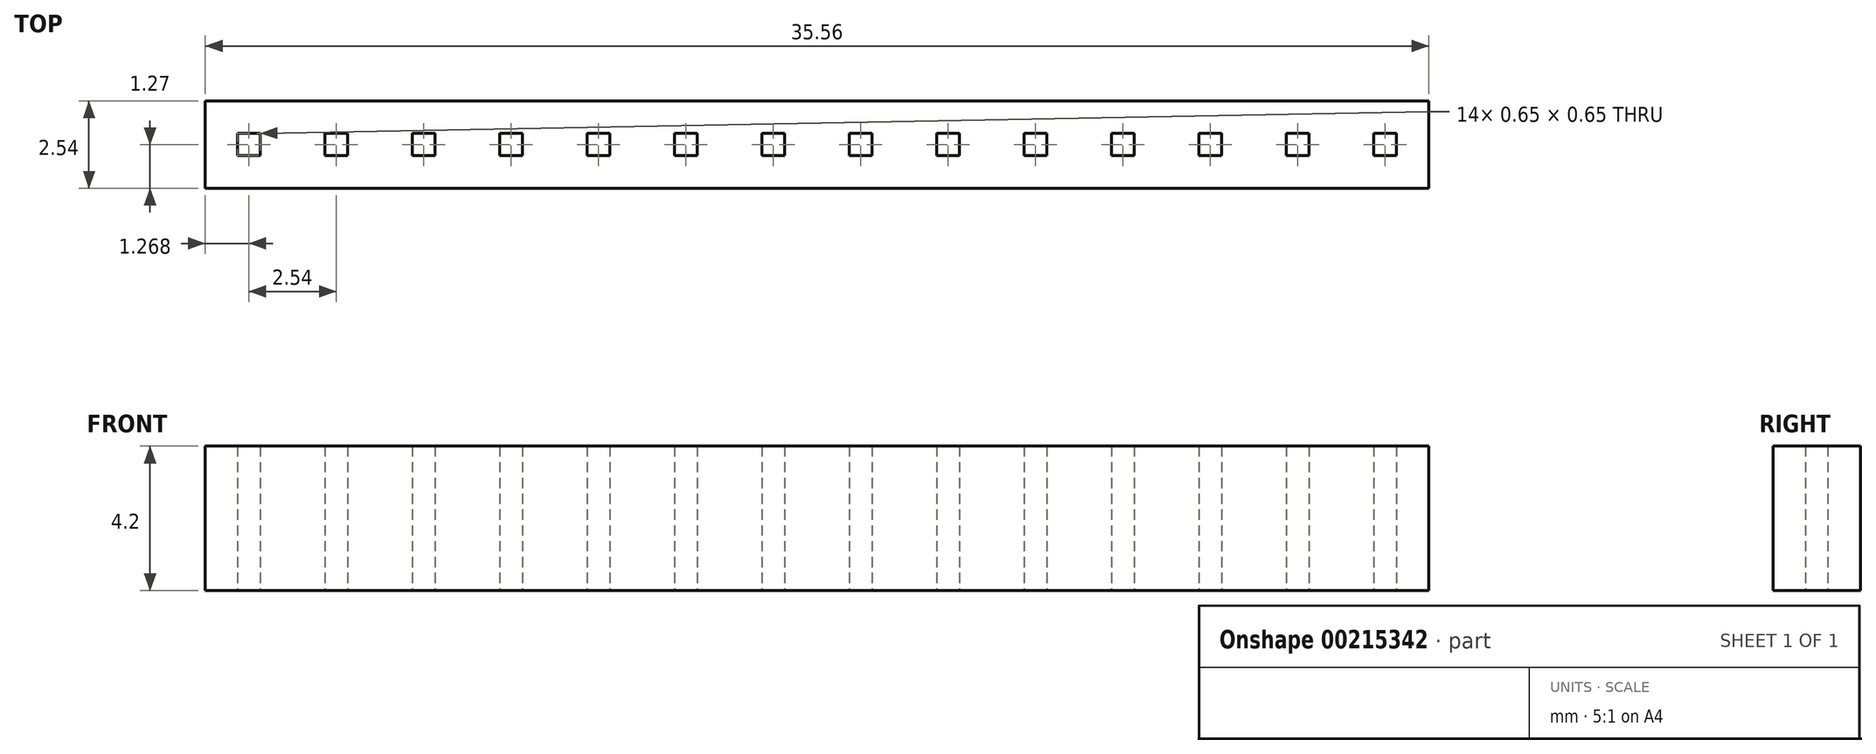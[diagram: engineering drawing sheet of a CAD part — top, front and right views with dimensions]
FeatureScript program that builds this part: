
annotation { "Feature Type Name" : "Feature", "Feature Type Description" : "" }
export const myFeature = defineFeature(function(context is Context, id is Id, definition is map)
    precondition{}
    {
        {
            var Q0;
            Q0=qCreatedBy(makeId("Top.planeOp"),FACE);
            var sketch = newSketch(context, id + "F0", { "sketchPlane" : qUnion([Q0])});
            skLineSegment(sketch, "E0.bottom", {"start": v(-68.73, 0) * mm, "end": v(-71.27, 0) * mm});
            skLineSegment(sketch, "E0.top", {"start": v(-68.73, 2.54) * mm, "end": v(-71.27, 2.54) * mm});
            skLineSegment(sketch, "E0.left", {"start": v(-68.73, 0) * mm, "end": v(-68.73, 2.54) * mm});
            skLineSegment(sketch, "E0.right", {"start": v(-71.27, 0) * mm, "end": v(-71.27, 2.54) * mm});
            skPoint(sketch, "E0.middle", {"position": v(-70, 1.27) * mm});
            skLineSegment(sketch, "E1.left", {"start": v(-68.73, 0.4) * mm, "end": v(-68.73, 1.6) * mm});
            skLineSegment(sketch, "E2.bottom", {"start": v(-70.33, 1.6) * mm, "end": v(-69.68, 1.6) * mm});
            skLineSegment(sketch, "E2.top", {"start": v(-70.33, 0.94) * mm, "end": v(-69.68, 0.94) * mm});
            skLineSegment(sketch, "E2.left", {"start": v(-70.33, 1.6) * mm, "end": v(-70.33, 0.94) * mm});
            skLineSegment(sketch, "E2.right", {"start": v(-69.68, 1.6) * mm, "end": v(-69.68, 0.94) * mm});
            skLineSegment(sketch, "E3.1.0.0", {"start": v(-66.2, 0) * mm, "end": v(-68.73, 0) * mm});
            skLineSegment(sketch, "E3.1.0.1", {"start": v(-66.2, 2.54) * mm, "end": v(-68.73, 2.54) * mm});
            skPoint(sketch, "E3.1.0.2", {"position": v(-67.46, 1.27) * mm});
            skLineSegment(sketch, "E3.1.0.3", {"start": v(-66.2, 0.4) * mm, "end": v(-66.2, 1.6) * mm});
            skPoint(sketch, "E3.1.0.4", {"position": v(-67.46, 1.27) * mm});
            skLineSegment(sketch, "E3.1.0.5", {"start": v(-66.2, 0) * mm, "end": v(-66.2, 2.54) * mm});
            skLineSegment(sketch, "E3.1.0.7", {"start": v(-67.14, 1.6) * mm, "end": v(-67.14, 0.94) * mm});
            skLineSegment(sketch, "E3.1.0.8", {"start": v(-67.79, 1.6) * mm, "end": v(-67.79, 0.94) * mm});
            skLineSegment(sketch, "E3.1.0.9", {"start": v(-67.79, 1.6) * mm, "end": v(-67.14, 1.6) * mm});
            skLineSegment(sketch, "E3.1.0.10", {"start": v(-67.79, 0.94) * mm, "end": v(-67.14, 0.94) * mm});
            skLineSegment(sketch, "E3.2.0.0", {"start": v(-63.65, 0) * mm, "end": v(-66.2, 0) * mm});
            skLineSegment(sketch, "E3.2.0.1", {"start": v(-63.65, 2.54) * mm, "end": v(-66.2, 2.54) * mm});
            skPoint(sketch, "E3.2.0.2", {"position": v(-64.92, 1.27) * mm});
            skLineSegment(sketch, "E3.2.0.3", {"start": v(-63.65, 0.4) * mm, "end": v(-63.65, 1.6) * mm});
            skPoint(sketch, "E3.2.0.4", {"position": v(-64.92, 1.27) * mm});
            skLineSegment(sketch, "E3.2.0.5", {"start": v(-63.65, 0) * mm, "end": v(-63.65, 2.54) * mm});
            skLineSegment(sketch, "E3.2.0.6", {"start": v(-66.2, 0) * mm, "end": v(-66.2, 2.54) * mm});
            skLineSegment(sketch, "E3.2.0.7", {"start": v(-64.6, 1.6) * mm, "end": v(-64.6, 0.94) * mm});
            skLineSegment(sketch, "E3.2.0.8", {"start": v(-65.25, 1.6) * mm, "end": v(-65.25, 0.94) * mm});
            skLineSegment(sketch, "E3.2.0.9", {"start": v(-65.25, 1.6) * mm, "end": v(-64.6, 1.6) * mm});
            skLineSegment(sketch, "E3.2.0.10", {"start": v(-65.25, 0.94) * mm, "end": v(-64.6, 0.94) * mm});
            skLineSegment(sketch, "E3.3.0.0", {"start": v(-61.11, 0) * mm, "end": v(-63.65, 0) * mm});
            skLineSegment(sketch, "E3.3.0.1", {"start": v(-61.11, 2.54) * mm, "end": v(-63.65, 2.54) * mm});
            skPoint(sketch, "E3.3.0.2", {"position": v(-62.38, 1.27) * mm});
            skLineSegment(sketch, "E3.3.0.3", {"start": v(-61.11, 0.4) * mm, "end": v(-61.11, 1.6) * mm});
            skPoint(sketch, "E3.3.0.4", {"position": v(-62.38, 1.27) * mm});
            skLineSegment(sketch, "E3.3.0.5", {"start": v(-61.11, 0) * mm, "end": v(-61.11, 2.54) * mm});
            skLineSegment(sketch, "E3.3.0.6", {"start": v(-63.65, 0) * mm, "end": v(-63.65, 2.54) * mm});
            skLineSegment(sketch, "E3.3.0.7", {"start": v(-62.06, 1.6) * mm, "end": v(-62.06, 0.94) * mm});
            skLineSegment(sketch, "E3.3.0.8", {"start": v(-62.7, 1.6) * mm, "end": v(-62.7, 0.94) * mm});
            skLineSegment(sketch, "E3.3.0.9", {"start": v(-62.7, 1.6) * mm, "end": v(-62.06, 1.6) * mm});
            skLineSegment(sketch, "E3.3.0.10", {"start": v(-62.7, 0.94) * mm, "end": v(-62.06, 0.94) * mm});
            skLineSegment(sketch, "E3.4.0.0", {"start": v(-58.57, 0) * mm, "end": v(-61.11, 0) * mm});
            skLineSegment(sketch, "E3.4.0.1", {"start": v(-58.57, 2.54) * mm, "end": v(-61.11, 2.54) * mm});
            skPoint(sketch, "E3.4.0.2", {"position": v(-59.84, 1.27) * mm});
            skLineSegment(sketch, "E3.4.0.3", {"start": v(-58.57, 0.4) * mm, "end": v(-58.57, 1.6) * mm});
            skPoint(sketch, "E3.4.0.4", {"position": v(-59.84, 1.27) * mm});
            skLineSegment(sketch, "E3.4.0.5", {"start": v(-58.57, 0) * mm, "end": v(-58.57, 2.54) * mm});
            skLineSegment(sketch, "E3.4.0.6", {"start": v(-61.11, 0) * mm, "end": v(-61.11, 2.54) * mm});
            skLineSegment(sketch, "E3.4.0.7", {"start": v(-59.52, 1.6) * mm, "end": v(-59.52, 0.94) * mm});
            skLineSegment(sketch, "E3.4.0.8", {"start": v(-60.17, 1.6) * mm, "end": v(-60.17, 0.94) * mm});
            skLineSegment(sketch, "E3.4.0.9", {"start": v(-60.17, 1.6) * mm, "end": v(-59.52, 1.6) * mm});
            skLineSegment(sketch, "E3.4.0.10", {"start": v(-60.17, 0.94) * mm, "end": v(-59.52, 0.94) * mm});
            skLineSegment(sketch, "E3.5.0.0", {"start": v(-56.03, 0) * mm, "end": v(-58.57, 0) * mm});
            skLineSegment(sketch, "E3.5.0.1", {"start": v(-56.03, 2.54) * mm, "end": v(-58.57, 2.54) * mm});
            skPoint(sketch, "E3.5.0.2", {"position": v(-57.3, 1.27) * mm});
            skLineSegment(sketch, "E3.5.0.3", {"start": v(-56.03, 0.4) * mm, "end": v(-56.03, 1.6) * mm});
            skPoint(sketch, "E3.5.0.4", {"position": v(-57.3, 1.27) * mm});
            skLineSegment(sketch, "E3.5.0.5", {"start": v(-56.03, 0) * mm, "end": v(-56.03, 2.54) * mm});
            skLineSegment(sketch, "E3.5.0.6", {"start": v(-58.57, 0) * mm, "end": v(-58.57, 2.54) * mm});
            skLineSegment(sketch, "E3.5.0.7", {"start": v(-56.98, 1.6) * mm, "end": v(-56.98, 0.94) * mm});
            skLineSegment(sketch, "E3.5.0.8", {"start": v(-57.63, 1.6) * mm, "end": v(-57.63, 0.94) * mm});
            skLineSegment(sketch, "E3.5.0.9", {"start": v(-57.63, 1.6) * mm, "end": v(-56.98, 1.6) * mm});
            skLineSegment(sketch, "E3.5.0.10", {"start": v(-57.63, 0.94) * mm, "end": v(-56.98, 0.94) * mm});
            skLineSegment(sketch, "E3.6.0.0", {"start": v(-53.5, 0) * mm, "end": v(-56.03, 0) * mm});
            skLineSegment(sketch, "E3.6.0.1", {"start": v(-53.5, 2.54) * mm, "end": v(-56.03, 2.54) * mm});
            skPoint(sketch, "E3.6.0.2", {"position": v(-54.76, 1.27) * mm});
            skLineSegment(sketch, "E3.6.0.3", {"start": v(-53.5, 0.4) * mm, "end": v(-53.5, 1.6) * mm});
            skPoint(sketch, "E3.6.0.4", {"position": v(-54.76, 1.27) * mm});
            skLineSegment(sketch, "E3.6.0.5", {"start": v(-53.5, 0) * mm, "end": v(-53.5, 2.54) * mm});
            skLineSegment(sketch, "E3.6.0.6", {"start": v(-56.03, 0) * mm, "end": v(-56.03, 2.54) * mm});
            skLineSegment(sketch, "E3.6.0.7", {"start": v(-54.44, 1.6) * mm, "end": v(-54.44, 0.94) * mm});
            skLineSegment(sketch, "E3.6.0.8", {"start": v(-55.09, 1.6) * mm, "end": v(-55.09, 0.94) * mm});
            skLineSegment(sketch, "E3.6.0.9", {"start": v(-55.09, 1.6) * mm, "end": v(-54.44, 1.6) * mm});
            skLineSegment(sketch, "E3.6.0.10", {"start": v(-55.09, 0.94) * mm, "end": v(-54.44, 0.94) * mm});
            skLineSegment(sketch, "E3.7.0.0", {"start": v(-50.95, 0) * mm, "end": v(-53.5, 0) * mm});
            skLineSegment(sketch, "E3.7.0.1", {"start": v(-50.95, 2.54) * mm, "end": v(-53.5, 2.54) * mm});
            skPoint(sketch, "E3.7.0.2", {"position": v(-52.22, 1.27) * mm});
            skLineSegment(sketch, "E3.7.0.3", {"start": v(-50.95, 0.4) * mm, "end": v(-50.95, 1.6) * mm});
            skPoint(sketch, "E3.7.0.4", {"position": v(-52.22, 1.27) * mm});
            skLineSegment(sketch, "E3.7.0.5", {"start": v(-50.95, 0) * mm, "end": v(-50.95, 2.54) * mm});
            skLineSegment(sketch, "E3.7.0.6", {"start": v(-53.5, 0) * mm, "end": v(-53.5, 2.54) * mm});
            skLineSegment(sketch, "E3.7.0.7", {"start": v(-51.9, 1.6) * mm, "end": v(-51.9, 0.94) * mm});
            skLineSegment(sketch, "E3.7.0.8", {"start": v(-52.55, 1.6) * mm, "end": v(-52.55, 0.94) * mm});
            skLineSegment(sketch, "E3.7.0.9", {"start": v(-52.55, 1.6) * mm, "end": v(-51.9, 1.6) * mm});
            skLineSegment(sketch, "E3.7.0.10", {"start": v(-52.55, 0.94) * mm, "end": v(-51.9, 0.94) * mm});
            skLineSegment(sketch, "E3.8.0.0", {"start": v(-48.41, 0) * mm, "end": v(-50.95, 0) * mm});
            skLineSegment(sketch, "E3.8.0.1", {"start": v(-48.41, 2.54) * mm, "end": v(-50.95, 2.54) * mm});
            skPoint(sketch, "E3.8.0.2", {"position": v(-49.68, 1.27) * mm});
            skLineSegment(sketch, "E3.8.0.3", {"start": v(-48.41, 0.4) * mm, "end": v(-48.41, 1.6) * mm});
            skPoint(sketch, "E3.8.0.4", {"position": v(-49.68, 1.27) * mm});
            skLineSegment(sketch, "E3.8.0.5", {"start": v(-48.41, 0) * mm, "end": v(-48.41, 2.54) * mm});
            skLineSegment(sketch, "E3.8.0.6", {"start": v(-50.95, 0) * mm, "end": v(-50.95, 2.54) * mm});
            skLineSegment(sketch, "E3.8.0.7", {"start": v(-49.36, 1.6) * mm, "end": v(-49.36, 0.94) * mm});
            skLineSegment(sketch, "E3.8.0.8", {"start": v(-50, 1.6) * mm, "end": v(-50, 0.94) * mm});
            skLineSegment(sketch, "E3.8.0.9", {"start": v(-50, 1.6) * mm, "end": v(-49.36, 1.6) * mm});
            skLineSegment(sketch, "E3.8.0.10", {"start": v(-50, 0.94) * mm, "end": v(-49.36, 0.94) * mm});
            skLineSegment(sketch, "E3.9.0.0", {"start": v(-45.87, 0) * mm, "end": v(-48.41, 0) * mm});
            skLineSegment(sketch, "E3.9.0.1", {"start": v(-45.87, 2.54) * mm, "end": v(-48.41, 2.54) * mm});
            skPoint(sketch, "E3.9.0.2", {"position": v(-47.14, 1.27) * mm});
            skLineSegment(sketch, "E3.9.0.3", {"start": v(-45.87, 0.4) * mm, "end": v(-45.87, 1.6) * mm});
            skPoint(sketch, "E3.9.0.4", {"position": v(-47.14, 1.27) * mm});
            skLineSegment(sketch, "E3.9.0.5", {"start": v(-45.87, 0) * mm, "end": v(-45.87, 2.54) * mm});
            skLineSegment(sketch, "E3.9.0.6", {"start": v(-48.41, 0) * mm, "end": v(-48.41, 2.54) * mm});
            skLineSegment(sketch, "E3.9.0.7", {"start": v(-46.82, 1.6) * mm, "end": v(-46.82, 0.94) * mm});
            skLineSegment(sketch, "E3.9.0.8", {"start": v(-47.47, 1.6) * mm, "end": v(-47.47, 0.94) * mm});
            skLineSegment(sketch, "E3.9.0.9", {"start": v(-47.47, 1.6) * mm, "end": v(-46.82, 1.6) * mm});
            skLineSegment(sketch, "E3.9.0.10", {"start": v(-47.47, 0.94) * mm, "end": v(-46.82, 0.94) * mm});
            skLineSegment(sketch, "E3.10.0.0", {"start": v(-43.33, 0) * mm, "end": v(-45.87, 0) * mm});
            skLineSegment(sketch, "E3.10.0.1", {"start": v(-43.33, 2.54) * mm, "end": v(-45.87, 2.54) * mm});
            skPoint(sketch, "E3.10.0.2", {"position": v(-44.6, 1.27) * mm});
            skLineSegment(sketch, "E3.10.0.3", {"start": v(-43.33, 0.4) * mm, "end": v(-43.33, 1.6) * mm});
            skPoint(sketch, "E3.10.0.4", {"position": v(-44.6, 1.27) * mm});
            skLineSegment(sketch, "E3.10.0.5", {"start": v(-43.33, 0) * mm, "end": v(-43.33, 2.54) * mm});
            skLineSegment(sketch, "E3.10.0.6", {"start": v(-45.87, 0) * mm, "end": v(-45.87, 2.54) * mm});
            skLineSegment(sketch, "E3.10.0.7", {"start": v(-44.28, 1.6) * mm, "end": v(-44.28, 0.94) * mm});
            skLineSegment(sketch, "E3.10.0.8", {"start": v(-44.93, 1.6) * mm, "end": v(-44.93, 0.94) * mm});
            skLineSegment(sketch, "E3.10.0.9", {"start": v(-44.93, 1.6) * mm, "end": v(-44.28, 1.6) * mm});
            skLineSegment(sketch, "E3.10.0.10", {"start": v(-44.93, 0.94) * mm, "end": v(-44.28, 0.94) * mm});
            skLineSegment(sketch, "E3.11.0.0", {"start": v(-40.8, 0) * mm, "end": v(-43.33, 0) * mm});
            skLineSegment(sketch, "E3.11.0.1", {"start": v(-40.8, 2.54) * mm, "end": v(-43.33, 2.54) * mm});
            skPoint(sketch, "E3.11.0.2", {"position": v(-42.06, 1.27) * mm});
            skLineSegment(sketch, "E3.11.0.3", {"start": v(-40.8, 0.4) * mm, "end": v(-40.8, 1.6) * mm});
            skPoint(sketch, "E3.11.0.4", {"position": v(-42.06, 1.27) * mm});
            skLineSegment(sketch, "E3.11.0.5", {"start": v(-40.8, 0) * mm, "end": v(-40.8, 2.54) * mm});
            skLineSegment(sketch, "E3.11.0.6", {"start": v(-43.33, 0) * mm, "end": v(-43.33, 2.54) * mm});
            skLineSegment(sketch, "E3.11.0.7", {"start": v(-41.74, 1.6) * mm, "end": v(-41.74, 0.94) * mm});
            skLineSegment(sketch, "E3.11.0.8", {"start": v(-42.39, 1.6) * mm, "end": v(-42.39, 0.94) * mm});
            skLineSegment(sketch, "E3.11.0.9", {"start": v(-42.39, 1.6) * mm, "end": v(-41.74, 1.6) * mm});
            skLineSegment(sketch, "E3.11.0.10", {"start": v(-42.39, 0.94) * mm, "end": v(-41.74, 0.94) * mm});
            skLineSegment(sketch, "E3.12.0.0", {"start": v(-38.25, 0) * mm, "end": v(-40.8, 0) * mm});
            skLineSegment(sketch, "E3.12.0.1", {"start": v(-38.25, 2.54) * mm, "end": v(-40.8, 2.54) * mm});
            skPoint(sketch, "E3.12.0.2", {"position": v(-39.52, 1.27) * mm});
            skLineSegment(sketch, "E3.12.0.3", {"start": v(-38.25, 0.4) * mm, "end": v(-38.25, 1.6) * mm});
            skPoint(sketch, "E3.12.0.4", {"position": v(-39.52, 1.27) * mm});
            skLineSegment(sketch, "E3.12.0.5", {"start": v(-38.25, 0) * mm, "end": v(-38.25, 2.54) * mm});
            skLineSegment(sketch, "E3.12.0.6", {"start": v(-40.8, 0) * mm, "end": v(-40.8, 2.54) * mm});
            skLineSegment(sketch, "E3.12.0.7", {"start": v(-39.2, 1.6) * mm, "end": v(-39.2, 0.94) * mm});
            skLineSegment(sketch, "E3.12.0.8", {"start": v(-39.85, 1.6) * mm, "end": v(-39.85, 0.94) * mm});
            skLineSegment(sketch, "E3.12.0.9", {"start": v(-39.85, 1.6) * mm, "end": v(-39.2, 1.6) * mm});
            skLineSegment(sketch, "E3.12.0.10", {"start": v(-39.85, 0.94) * mm, "end": v(-39.2, 0.94) * mm});
            skLineSegment(sketch, "E3.13.0.0", {"start": v(-35.71, 0) * mm, "end": v(-38.25, 0) * mm});
            skLineSegment(sketch, "E3.13.0.1", {"start": v(-35.71, 2.54) * mm, "end": v(-38.25, 2.54) * mm});
            skPoint(sketch, "E3.13.0.2", {"position": v(-36.98, 1.27) * mm});
            skLineSegment(sketch, "E3.13.0.3", {"start": v(-35.71, 0.4) * mm, "end": v(-35.71, 1.6) * mm});
            skPoint(sketch, "E3.13.0.4", {"position": v(-36.98, 1.27) * mm});
            skLineSegment(sketch, "E3.13.0.5", {"start": v(-35.71, 0) * mm, "end": v(-35.71, 2.54) * mm});
            skLineSegment(sketch, "E3.13.0.6", {"start": v(-38.25, 0) * mm, "end": v(-38.25, 2.54) * mm});
            skLineSegment(sketch, "E3.13.0.7", {"start": v(-36.66, 1.6) * mm, "end": v(-36.66, 0.94) * mm});
            skLineSegment(sketch, "E3.13.0.8", {"start": v(-37.3, 1.6) * mm, "end": v(-37.3, 0.94) * mm});
            skLineSegment(sketch, "E3.13.0.9", {"start": v(-37.3, 1.6) * mm, "end": v(-36.66, 1.6) * mm});
            skLineSegment(sketch, "E3.13.0.10", {"start": v(-37.3, 0.94) * mm, "end": v(-36.66, 0.94) * mm});
            skLineSegment(sketch, "E3.direction1", {"start": v(-71.27, 0) * mm, "end": v(-68.73, 0) * mm, "construction": true});
            skSolve(sketch);
        }
        {
            var Q0;
            Q0 = qSketchRegion(id + "F0", true);
            extrude(context, id + "F1", {"entities" : qUnion([Q0]), "depth" : 4.2 * mm});
        }
    });
